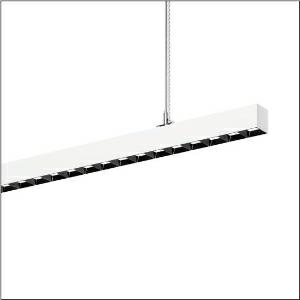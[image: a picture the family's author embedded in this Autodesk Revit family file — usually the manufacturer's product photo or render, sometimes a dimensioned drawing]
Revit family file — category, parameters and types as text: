
# Revit family: silica_21_51mx31tctdw
name_source: partatom
category: Lighting Fixtures
units: mm (PartAtom-declared; Revit-internal decimal feet)

## family parameters
Cut with Voids When Loaded = No
Host = Face
Light Source = No
Part Type = Normal
Room Calculation Point = No
Round Connector Dimension = Use Diameter
Shared = No

## types (1)
- --- (1 x LED, 15550 lm, 133.9 W, 6500K)
    Apparent Load = 134 VA
    CIE Flux Codes = 85 99 100 60 100
    Color Rendering = 80
    Color Temperature = 6500K
    Default Elevation = 1800 mm
    Description = Silica 21, office luminaire, primary light control with darklight reflector, of PMMA, black, CAT 2 (L<= 3000cd/m²), light emission: direct/indirect distribution, primary light characteristic: symmetric, installation type: suspended mounting, LED, rated luminous flux: 15.550lm, luminous efficacy: 111lm/W, light colour: 8tw, colour temperature: 2700..6500K, control gear: DALI DT8, with terminal, 3+2-pole, max. 2.5mm², mains connection: 220..240V, AC, 50/60Hz, rated input power: 140.6W, luminaire housing, of aluminium, traffic white (RAL 9016), length: 3.004mm, width: 53mm, height: 53mm, protection rating (complete): IP20, insulation class (complete): insulation class I (protective earthing), certification: CE, permissible operating ambient temperature: 0..+35°C, standard: EN 50419, packaging unit: 1 piece
    Height = 53 mm
    Lamp = 1 x LED
    Lamp Light Flux = 15550 lm
    Lamp Power = 133.9 W
    Lamp count = 1
    Length = 3004 mm
    Luminous efficacy = 116 lm/W
    Manufacturer = Siteco
    ModVariant = No
    Model = 51MX31TCTDW
    Mounting Place = Ceiling
    Mounting Type = Pendant
    Number of Poles = 1
    OnlyDefault = Yes
    Power Factor = 1
    Product Name = Silica 21
    Product group = office luminaire | ceiling pendant
    ProductGroupID = 903
    Protection Class = Protection class I
    Protection Degree = IP 20
    RLX_Detail_Level = 1
    RLX_Emergency_Light_Flux = 0 lm
    RLX_Emergency_Type = 0
    RLX_Emergency_Type_DB = No
    RlxData = <blob elided: 60805 chars, md5=e23bdaad>
    Socket = socket
    Standby Power = 0 W
    System Light Flux = 15550 lm
    System Power = 134 W
    Type Comments = individual setting
    Type Image = l_1335871.jpg
    URL = http://relux.com
    VarID = @adj_139391
    Voltage = 0 V
    Weight = 0.00 kg
    Width = 53 mm

## geometry (parser evidence)
native form markers: Blend x4, Sweep x15
no freeform markers — native parametric forms only
